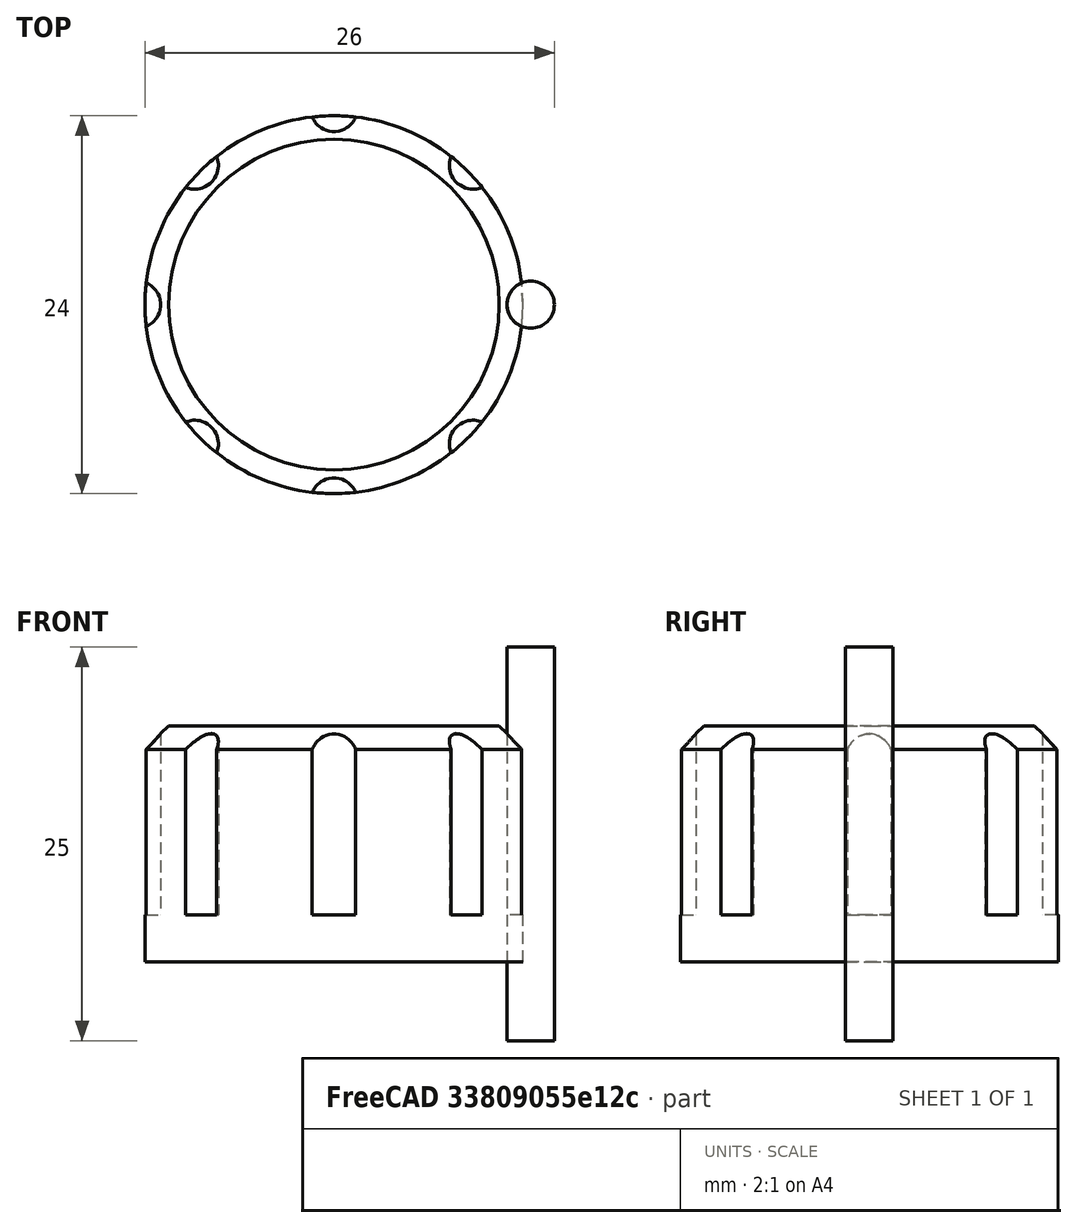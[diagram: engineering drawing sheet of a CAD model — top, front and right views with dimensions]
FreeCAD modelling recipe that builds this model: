
FCSTD DOCUMENT  (FreeCAD 0.21R33771 (Git))
Label: OJT1_T12R01_boto seleccio
License: All rights reserved
LicenseURL: http://en.wikipedia.org/wiki/All_rights_reserved
objects: Part::Cylinder×2, Part::FeaturePython×1, Part::Chamfer×1, Part::Cut×1
note: 4 computed .brp shape members not serialized (recipe doc carries the construction recipe); baked Part::Feature solids carry a one-line shape summary decoded from their .brp

FEATURE [Part::Cylinder] Cylinder
  Angle = 360
  AttacherType = Attacher::AttachEngine3D
  FirstAngle = 0
  Height = 15
  Radius = 12
  SecondAngle = 0
FEATURE [Part::Cylinder] Cylinder001
  Angle = 360
  AttacherType = Attacher::AttachEngine3D
  FirstAngle = 0
  Height = 25
  Placement = pos=(12.5,0,-5) rot=(0,0,1;0rad)
  Radius = 1.5
  SecondAngle = 0
FEATURE [Part::FeaturePython] Array  # Draft array (typed FeaturePython)
  AlwaysSyncPlacement = false
  Angle = 360
  ArrayType = 1
  Axis = (0,0,0)
  Base = -> Cylinder001
  Center = (0,0,0)
  Count = 8
  ExpandArray = false
  Fuse = false
  IntervalAxis = (0,0,0)
  IntervalX = (50,0,0)
  IntervalY = (0,50,0)
  IntervalZ = (0,0,50)
  NumberCircles = 3
  NumberPolar = 8
  NumberX = 2
  NumberY = 2
  NumberZ = 1
  Placement = pos=(0,0,8) rot=(0,0,1;0rad)
  PlacementList = 8 placements: [(12.5,0,-5),(8.83883,8.83883,-5),(2.77556e-15,12.5,-5),(-8.83883,8.83883,-5),(-12.5,1.53081e-15,-5),(-8.83883,-8.83883,-5),(-2.77556e-15,-12.5,-5),(8.83883,-8.83883,-5)]
  RadialDistance = 50
  ScaleList = (8) [(1,1,1),(1,1,1),(1,1,1),(1,1,1),(1,1,1),(1,1,1),(1,1,1),(1,1,1)]
  Symmetry = 1
  TangentialDistance = 25
FEATURE [Part::Chamfer] Chamfer
  Base = -> Cylinder
  Edges = 1 edges r=1.5: [Edge3]
FEATURE [Part::Cut] Cut  label="boto"
  Base = -> Chamfer
  Refine = true
  Tool = -> Array
